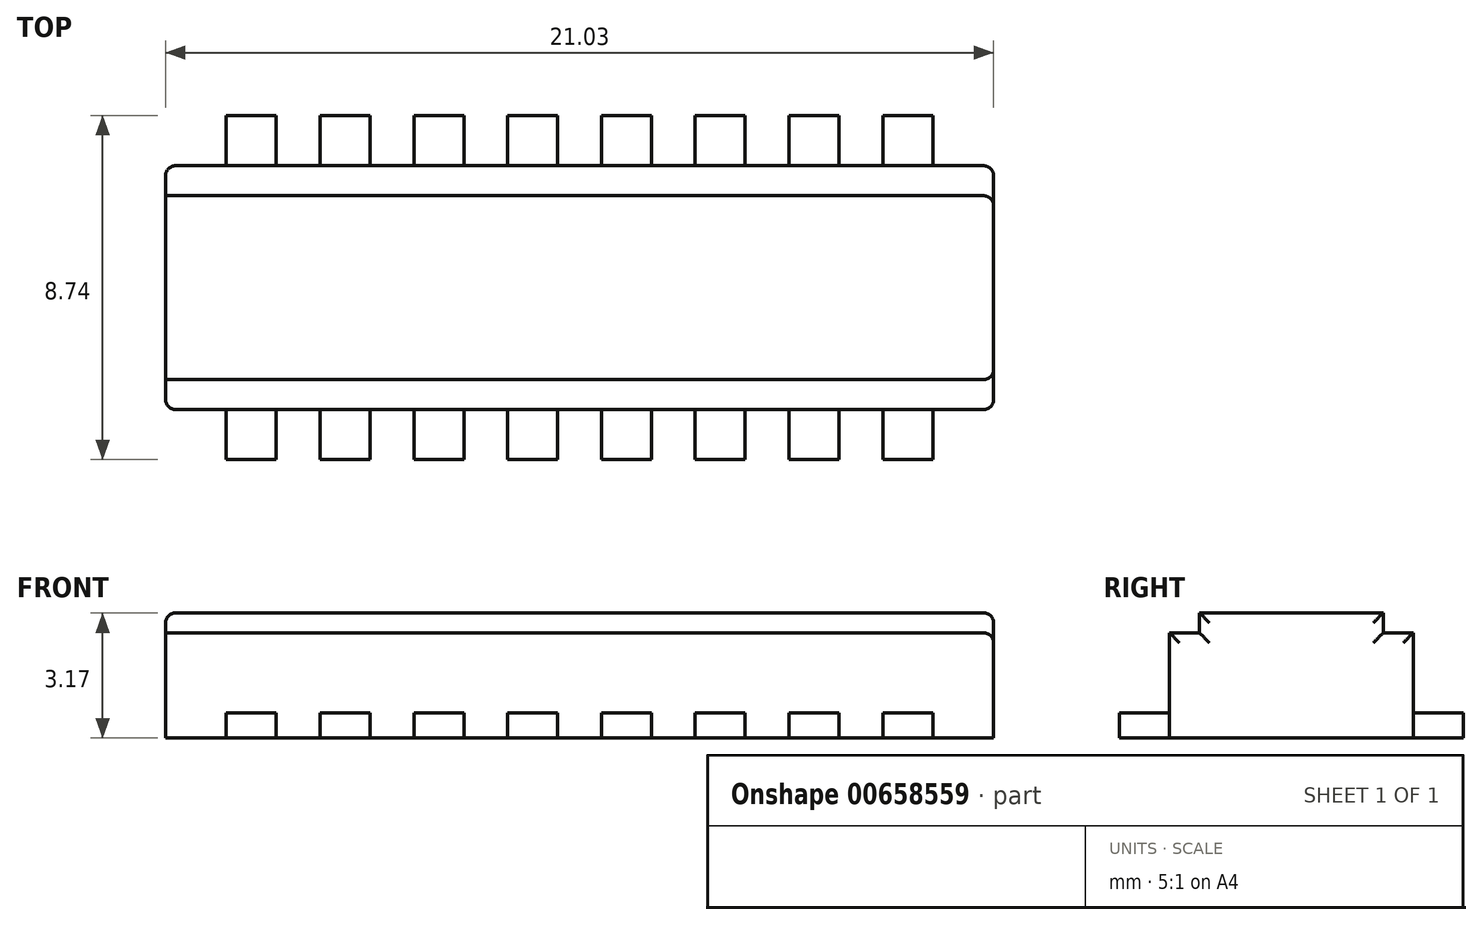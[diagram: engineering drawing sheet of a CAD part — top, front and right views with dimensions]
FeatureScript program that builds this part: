
annotation { "Feature Type Name" : "Feature", "Feature Type Description" : "" }
export const myFeature = defineFeature(function(context is Context, id is Id, definition is map)
    precondition{}
    {
        {
            var Q0;
            Q0=qCreatedBy(makeId("Top.planeOp"),FACE);
            var sketch = newSketch(context, id + "F0", { "sketchPlane" : qUnion([Q0])});
            skLineSegment(sketch, "E0.bottom", {"start": v(-9.13, 1.83) * mm, "end": v(11.9, 1.83) * mm});
            skLineSegment(sketch, "E0.top", {"start": v(-9.13, -4.37) * mm, "end": v(11.9, -4.37) * mm});
            skLineSegment(sketch, "E0.left", {"start": v(-9.13, 1.83) * mm, "end": v(-9.13, -4.37) * mm});
            skLineSegment(sketch, "E0.right", {"start": v(11.9, 1.83) * mm, "end": v(11.9, -4.37) * mm});
            skSolve(sketch);
        }
        {
            var Q0;
            Q0=qSketchRegion(id+"F0",true);
            extrude(context, id + "F1", {"entities" : qUnion([Q0]), "depth" : 3.17 * mm, "offsetDistance" : 25.4 * mm});
        }
        {
            var Q0;
            Q0=qCreatedBy(makeId("Top.planeOp"),FACE);
            var sketch = newSketch(context, id + "F2", { "sketchPlane" : qUnion([Q0])});
            skLineSegment(sketch, "E1.bottom", {"start": v(-7.59, 3.1) * mm, "end": v(-6.32, 3.1) * mm});
            skLineSegment(sketch, "E1.top", {"start": v(-7.59, 1.83) * mm, "end": v(-6.32, 1.83) * mm});
            skLineSegment(sketch, "E1.left", {"start": v(-7.59, 3.1) * mm, "end": v(-7.59, 1.83) * mm});
            skLineSegment(sketch, "E1.right", {"start": v(-6.32, 3.1) * mm, "end": v(-6.32, 1.83) * mm});
            skLineSegment(sketch, "E2.1.0.0", {"start": v(-3.93, 3.1) * mm, "end": v(-3.93, 1.83) * mm});
            skLineSegment(sketch, "E2.1.0.1", {"start": v(-5.2, 3.1) * mm, "end": v(-5.2, 1.83) * mm});
            skLineSegment(sketch, "E2.1.0.2", {"start": v(-5.2, 1.83) * mm, "end": v(-3.93, 1.83) * mm});
            skLineSegment(sketch, "E2.1.0.3", {"start": v(-5.2, 3.1) * mm, "end": v(-3.93, 3.1) * mm});
            skLineSegment(sketch, "E2.2.0.0", {"start": v(-1.55, 3.1) * mm, "end": v(-1.55, 1.83) * mm});
            skLineSegment(sketch, "E2.2.0.1", {"start": v(-2.82, 3.1) * mm, "end": v(-2.82, 1.83) * mm});
            skLineSegment(sketch, "E2.2.0.2", {"start": v(-2.82, 1.83) * mm, "end": v(-1.55, 1.83) * mm});
            skLineSegment(sketch, "E2.2.0.3", {"start": v(-2.82, 3.1) * mm, "end": v(-1.55, 3.1) * mm});
            skLineSegment(sketch, "E2.3.0.0", {"start": v(0.83, 3.1) * mm, "end": v(0.83, 1.83) * mm});
            skLineSegment(sketch, "E2.3.0.1", {"start": v(-0.44, 3.1) * mm, "end": v(-0.44, 1.83) * mm});
            skLineSegment(sketch, "E2.3.0.2", {"start": v(-0.44, 1.83) * mm, "end": v(0.83, 1.83) * mm});
            skLineSegment(sketch, "E2.3.0.3", {"start": v(-0.44, 3.1) * mm, "end": v(0.83, 3.1) * mm});
            skLineSegment(sketch, "E2.4.0.0", {"start": v(3.21, 3.1) * mm, "end": v(3.21, 1.83) * mm});
            skLineSegment(sketch, "E2.4.0.1", {"start": v(1.94, 3.1) * mm, "end": v(1.94, 1.83) * mm});
            skLineSegment(sketch, "E2.4.0.2", {"start": v(1.94, 1.83) * mm, "end": v(3.21, 1.83) * mm});
            skLineSegment(sketch, "E2.4.0.3", {"start": v(1.94, 3.1) * mm, "end": v(3.21, 3.1) * mm});
            skLineSegment(sketch, "E2.5.0.0", {"start": v(5.6, 3.1) * mm, "end": v(5.6, 1.83) * mm});
            skLineSegment(sketch, "E2.5.0.1", {"start": v(4.33, 3.1) * mm, "end": v(4.33, 1.83) * mm});
            skLineSegment(sketch, "E2.5.0.2", {"start": v(4.33, 1.83) * mm, "end": v(5.6, 1.83) * mm});
            skLineSegment(sketch, "E2.5.0.3", {"start": v(4.33, 3.1) * mm, "end": v(5.6, 3.1) * mm});
            skLineSegment(sketch, "E2.6.0.0", {"start": v(7.98, 3.1) * mm, "end": v(7.98, 1.83) * mm});
            skLineSegment(sketch, "E2.6.0.1", {"start": v(6.7, 3.1) * mm, "end": v(6.7, 1.83) * mm});
            skLineSegment(sketch, "E2.6.0.2", {"start": v(6.7, 1.83) * mm, "end": v(7.98, 1.83) * mm});
            skLineSegment(sketch, "E2.6.0.3", {"start": v(6.7, 3.1) * mm, "end": v(7.98, 3.1) * mm});
            skLineSegment(sketch, "E2.direction1", {"start": v(-7.59, 1.83) * mm, "end": v(-5.2, 1.83) * mm, "construction": true});
            skLineSegment(sketch, "E3.bottom", {"start": v(-7.59, -4.37) * mm, "end": v(-6.32, -4.37) * mm});
            skLineSegment(sketch, "E3.top", {"start": v(-7.59, -5.64) * mm, "end": v(-6.32, -5.64) * mm});
            skLineSegment(sketch, "E3.left", {"start": v(-7.59, -4.37) * mm, "end": v(-7.59, -5.64) * mm});
            skLineSegment(sketch, "E3.right", {"start": v(-6.32, -4.37) * mm, "end": v(-6.32, -5.64) * mm});
            skLineSegment(sketch, "E4.1.0.0", {"start": v(-5.2, -5.64) * mm, "end": v(-3.93, -5.64) * mm});
            skLineSegment(sketch, "E4.1.0.1", {"start": v(-5.2, -4.37) * mm, "end": v(-5.2, -5.64) * mm});
            skLineSegment(sketch, "E4.1.0.2", {"start": v(-5.2, -4.37) * mm, "end": v(-3.93, -4.37) * mm});
            skLineSegment(sketch, "E4.1.0.3", {"start": v(-3.93, -4.37) * mm, "end": v(-3.93, -5.64) * mm});
            skLineSegment(sketch, "E4.2.0.0", {"start": v(-2.82, -5.64) * mm, "end": v(-1.55, -5.64) * mm});
            skLineSegment(sketch, "E4.2.0.1", {"start": v(-2.82, -4.37) * mm, "end": v(-2.82, -5.64) * mm});
            skLineSegment(sketch, "E4.2.0.2", {"start": v(-2.82, -4.37) * mm, "end": v(-1.55, -4.37) * mm});
            skLineSegment(sketch, "E4.2.0.3", {"start": v(-1.55, -4.37) * mm, "end": v(-1.55, -5.64) * mm});
            skLineSegment(sketch, "E4.3.0.0", {"start": v(-0.44, -5.64) * mm, "end": v(0.83, -5.64) * mm});
            skLineSegment(sketch, "E4.3.0.1", {"start": v(-0.44, -4.37) * mm, "end": v(-0.44, -5.64) * mm});
            skLineSegment(sketch, "E4.3.0.2", {"start": v(-0.44, -4.37) * mm, "end": v(0.83, -4.37) * mm});
            skLineSegment(sketch, "E4.3.0.3", {"start": v(0.83, -4.37) * mm, "end": v(0.83, -5.64) * mm});
            skLineSegment(sketch, "E4.4.0.0", {"start": v(1.94, -5.64) * mm, "end": v(3.21, -5.64) * mm});
            skLineSegment(sketch, "E4.4.0.1", {"start": v(1.94, -4.37) * mm, "end": v(1.94, -5.64) * mm});
            skLineSegment(sketch, "E4.4.0.2", {"start": v(1.94, -4.37) * mm, "end": v(3.21, -4.37) * mm});
            skLineSegment(sketch, "E4.4.0.3", {"start": v(3.21, -4.37) * mm, "end": v(3.21, -5.64) * mm});
            skLineSegment(sketch, "E4.5.0.0", {"start": v(4.33, -5.64) * mm, "end": v(5.6, -5.64) * mm});
            skLineSegment(sketch, "E4.5.0.1", {"start": v(4.33, -4.37) * mm, "end": v(4.33, -5.64) * mm});
            skLineSegment(sketch, "E4.5.0.2", {"start": v(4.33, -4.37) * mm, "end": v(5.6, -4.37) * mm});
            skLineSegment(sketch, "E4.5.0.3", {"start": v(5.6, -4.37) * mm, "end": v(5.6, -5.64) * mm});
            skLineSegment(sketch, "E4.6.0.0", {"start": v(6.7, -5.64) * mm, "end": v(7.98, -5.64) * mm});
            skLineSegment(sketch, "E4.6.0.1", {"start": v(6.7, -4.37) * mm, "end": v(6.7, -5.64) * mm});
            skLineSegment(sketch, "E4.6.0.2", {"start": v(6.7, -4.37) * mm, "end": v(7.98, -4.37) * mm});
            skLineSegment(sketch, "E4.6.0.3", {"start": v(7.98, -4.37) * mm, "end": v(7.98, -5.64) * mm});
            skLineSegment(sketch, "E4.direction1", {"start": v(-7.59, -5.64) * mm, "end": v(-5.2, -5.64) * mm, "construction": true});
            skLineSegment(sketch, "E5.0.7.0", {"start": v(10.36, 3.1) * mm, "end": v(10.36, 1.83) * mm});
            skLineSegment(sketch, "E5.3.7.0", {"start": v(9.1, 3.1) * mm, "end": v(9.1, 1.83) * mm});
            skLineSegment(sketch, "E5.6.7.0", {"start": v(9.1, 1.83) * mm, "end": v(10.36, 1.83) * mm});
            skLineSegment(sketch, "E5.9.7.0", {"start": v(9.1, 3.1) * mm, "end": v(10.36, 3.1) * mm});
            skLineSegment(sketch, "E6.0.7.0", {"start": v(9.1, -5.64) * mm, "end": v(10.36, -5.64) * mm});
            skLineSegment(sketch, "E6.3.7.0", {"start": v(9.1, -4.37) * mm, "end": v(9.1, -5.64) * mm});
            skLineSegment(sketch, "E6.6.7.0", {"start": v(9.1, -4.37) * mm, "end": v(10.36, -4.37) * mm});
            skLineSegment(sketch, "E6.9.7.0", {"start": v(10.36, -4.37) * mm, "end": v(10.36, -5.64) * mm});
            skSolve(sketch);
        }
        {
            var Q0;
            Q0=qSketchRegion(id+"F2",true);
            extrude(context, id + "F3", {"entities" : qUnion([Q0]), "operationType" : NewBodyOperationType.ADD, "depth" : 0.64 * mm, "offsetDistance" : 25.4 * mm});
        }
        {
            var Q0;
            Q0=makeQuery(id+"F1.opExtrude","SWEPT_FACE",FACE,{"disambiguationData":[OSD([sQuery(id+"F0.wireOp",EDGE,"E0.left")])]});
            var sketch = newSketch(context, id + "F4", { "sketchPlane" : qUnion([Q0])});
            skSolve(sketch);
        }
        {
            var Q0;
            {var subQ0=sQuery(id+"F0.wireOp",EDGE,"E0.left");Q0=makeQuery(id+"F4.imprint","IMPRINT",FACE,{"disambiguationData":[TD([[makeQuery(id+"F4.imprint","IMPRINT",EDGE,{"derivedFrom":makeQuery(id+"F1.opExtrude","CAP_EDGE",EDGE,{"disambiguationData":[OSD([subQ0])],"isStart":true})}),1.0]])]});}
            var sketch = newSketch(context, id + "F5", { "sketchPlane" : qUnion([Q0])});
            skLineSegment(sketch, "E7.bottom", {"start": v(-1.83, 3.18) * mm, "end": v(-1.06, 3.18) * mm});
            skLineSegment(sketch, "E7.top", {"start": v(-1.83, 2.67) * mm, "end": v(-1.06, 2.67) * mm});
            skLineSegment(sketch, "E7.left", {"start": v(-1.83, 3.18) * mm, "end": v(-1.83, 2.67) * mm});
            skLineSegment(sketch, "E7.right", {"start": v(-1.06, 3.18) * mm, "end": v(-1.06, 2.67) * mm});
            skLineSegment(sketch, "E8.bottom", {"start": v(4.37, 3.18) * mm, "end": v(3.6, 3.18) * mm});
            skLineSegment(sketch, "E8.top", {"start": v(4.37, 2.67) * mm, "end": v(3.6, 2.67) * mm});
            skLineSegment(sketch, "E8.left", {"start": v(4.37, 3.18) * mm, "end": v(4.37, 2.67) * mm});
            skLineSegment(sketch, "E8.right", {"start": v(3.6, 3.18) * mm, "end": v(3.6, 2.67) * mm});
            skSolve(sketch);
        }
        {
            var Q0;
            Q0=qSketchRegion(id+"F5",true);
            extrude(context, id + "F6", {"entities" : qUnion([Q0]), "operationType" : NewBodyOperationType.REMOVE, "oppositeDirection" : true, "depth" : 25.4 * mm, "offsetDistance" : 25.4 * mm});
        }
        {
            var Q0;
            Q0=makeQuery(id+"F6.boolean.opBoolean","COPY",EDGE,{"derivedFrom":makeQuery(id+"F6.opExtrude","SWEPT_EDGE",EDGE,{"disambiguationData":[OSD([sQuery(id+"F0.wireOp",EDGE,"E0.bottom"),sQuery(id+"F0.wireOp",EDGE,"E0.left"),sQuery(id+"F5.wireOp",EDGE,"E7.top"),sQuery(id+"F5.wireOp",EDGE,"E7.left")])]})});
            var Q1;
            Q1=makeQuery(id+"F6.boolean.opBoolean","COPY",EDGE,{"derivedFrom":makeQuery(id+"F6.opExtrude","SWEPT_EDGE",EDGE,{"disambiguationData":[OSD([sQuery(id+"F0.wireOp",EDGE,"E0.left"),sQuery(id+"F5.wireOp",EDGE,"E7.bottom"),sQuery(id+"F5.wireOp",EDGE,"E7.right")])]})});
            var Q2;
            Q2=makeQuery(id+"F6.boolean.opBoolean","COPY",EDGE,{"derivedFrom":makeQuery(id+"F6.opExtrude","SWEPT_EDGE",EDGE,{"disambiguationData":[OSD([sQuery(id+"F0.wireOp",EDGE,"E0.left"),sQuery(id+"F5.wireOp",EDGE,"E8.bottom"),sQuery(id+"F5.wireOp",EDGE,"E8.right")])]})});
            var Q3;
            Q3=makeQuery(id+"F6.boolean.opBoolean","COPY",EDGE,{"derivedFrom":makeQuery(id+"F6.opExtrude","SWEPT_EDGE",EDGE,{"disambiguationData":[OSD([sQuery(id+"F0.wireOp",EDGE,"E0.top"),sQuery(id+"F0.wireOp",EDGE,"E0.left"),sQuery(id+"F5.wireOp",EDGE,"E8.top"),sQuery(id+"F5.wireOp",EDGE,"E8.left")])]})});
            var Q4;
            Q4=makeQuery(id+"F1.opExtrude","CAP_EDGE",EDGE,{"disambiguationData":[OSD([sQuery(id+"F0.wireOp",EDGE,"E0.left")])],"isStart":false});
            var Q5;
            Q5=makeQuery(id+"F6.boolean.opBoolean","COPY",EDGE,{"derivedFrom":makeQuery(id+"F6.opExtrude","CAP_EDGE",EDGE,{"disambiguationData":[OSD([sQuery(id+"F5.wireOp",EDGE,"E8.right")])],"isStart":true})});
            var Q6;
            Q6=makeQuery(id+"F6.boolean.opBoolean","COPY",EDGE,{"derivedFrom":makeQuery(id+"F6.opExtrude","CAP_EDGE",EDGE,{"disambiguationData":[OSD([sQuery(id+"F5.wireOp",EDGE,"E8.top")])],"isStart":true})});
            var Q7;
            Q7=makeQuery(id+"F1.opExtrude","SWEPT_EDGE",EDGE,{"disambiguationData":[OSD([sQuery(id+"F0.wireOp",EDGE,"E0.top"),sQuery(id+"F0.wireOp",EDGE,"E0.left")])]});
            var Q8;
            Q8=makeQuery(id+"F6.boolean.opBoolean","COPY",EDGE,{"derivedFrom":makeQuery(id+"F6.opExtrude","CAP_EDGE",EDGE,{"disambiguationData":[OSD([sQuery(id+"F5.wireOp",EDGE,"E7.top")])],"isStart":true})});
            var Q9;
            Q9=makeQuery(id+"F6.boolean.opBoolean","COPY",EDGE,{"derivedFrom":makeQuery(id+"F6.opExtrude","CAP_EDGE",EDGE,{"disambiguationData":[OSD([sQuery(id+"F5.wireOp",EDGE,"E7.right")])],"isStart":true})});
            var Q10;
            Q10=makeQuery(id+"F1.opExtrude","SWEPT_EDGE",EDGE,{"disambiguationData":[OSD([sQuery(id+"F0.wireOp",EDGE,"E0.bottom"),sQuery(id+"F0.wireOp",EDGE,"E0.left")])]});
            var Q11;
            Q11=makeQuery(id+"F1.opExtrude","SWEPT_EDGE",EDGE,{"disambiguationData":[OSD([sQuery(id+"F0.wireOp",EDGE,"E0.top"),sQuery(id+"F0.wireOp",EDGE,"E0.right")])]});
            var Q12;
            Q12=makeQuery(id+"F6.boolean.opBoolean","INTERSECT",EDGE,{"derivedFrom":[makeQuery(id+"F1.opExtrude","SWEPT_FACE",FACE,{"disambiguationData":[OSD([sQuery(id+"F0.wireOp",EDGE,"E0.right")])]}),makeQuery(id+"F6.opExtrude","SWEPT_FACE",FACE,{"disambiguationData":[OSD([sQuery(id+"F5.wireOp",EDGE,"E8.top")])]})]});
            var Q13;
            Q13=makeQuery(id+"F6.boolean.opBoolean","INTERSECT",EDGE,{"derivedFrom":[makeQuery(id+"F1.opExtrude","SWEPT_FACE",FACE,{"disambiguationData":[OSD([sQuery(id+"F0.wireOp",EDGE,"E0.right")])]}),makeQuery(id+"F6.opExtrude","SWEPT_FACE",FACE,{"disambiguationData":[OSD([sQuery(id+"F5.wireOp",EDGE,"E8.right")])]})]});
            var Q14;
            Q14=makeQuery(id+"F1.opExtrude","CAP_EDGE",EDGE,{"disambiguationData":[OSD([sQuery(id+"F0.wireOp",EDGE,"E0.right")])],"isStart":false});
            var Q15;
            Q15=makeQuery(id+"F6.boolean.opBoolean","INTERSECT",EDGE,{"derivedFrom":[makeQuery(id+"F1.opExtrude","SWEPT_FACE",FACE,{"disambiguationData":[OSD([sQuery(id+"F0.wireOp",EDGE,"E0.right")])]}),makeQuery(id+"F6.opExtrude","SWEPT_FACE",FACE,{"disambiguationData":[OSD([sQuery(id+"F5.wireOp",EDGE,"E7.right")])]})]});
            var Q16;
            Q16=makeQuery(id+"F6.boolean.opBoolean","INTERSECT",EDGE,{"derivedFrom":[makeQuery(id+"F1.opExtrude","SWEPT_FACE",FACE,{"disambiguationData":[OSD([sQuery(id+"F0.wireOp",EDGE,"E0.right")])]}),makeQuery(id+"F6.opExtrude","SWEPT_FACE",FACE,{"disambiguationData":[OSD([sQuery(id+"F5.wireOp",EDGE,"E7.top")])]})]});
            var Q17;
            Q17=makeQuery(id+"F1.opExtrude","SWEPT_EDGE",EDGE,{"disambiguationData":[OSD([sQuery(id+"F0.wireOp",EDGE,"E0.bottom"),sQuery(id+"F0.wireOp",EDGE,"E0.right")])]});
            fillet(context, id + "F7", {"entities" : qUnion([Q0, Q1, Q2, Q3, Q4, Q5, Q6, Q7, Q8, Q9, Q10, Q11, Q12, Q13, Q14, Q15, Q16, Q17]), "radius" : 0.25 * mm, "tangentPropagation" : true, "allowEdgeOverflow" : false});
        }
    });
